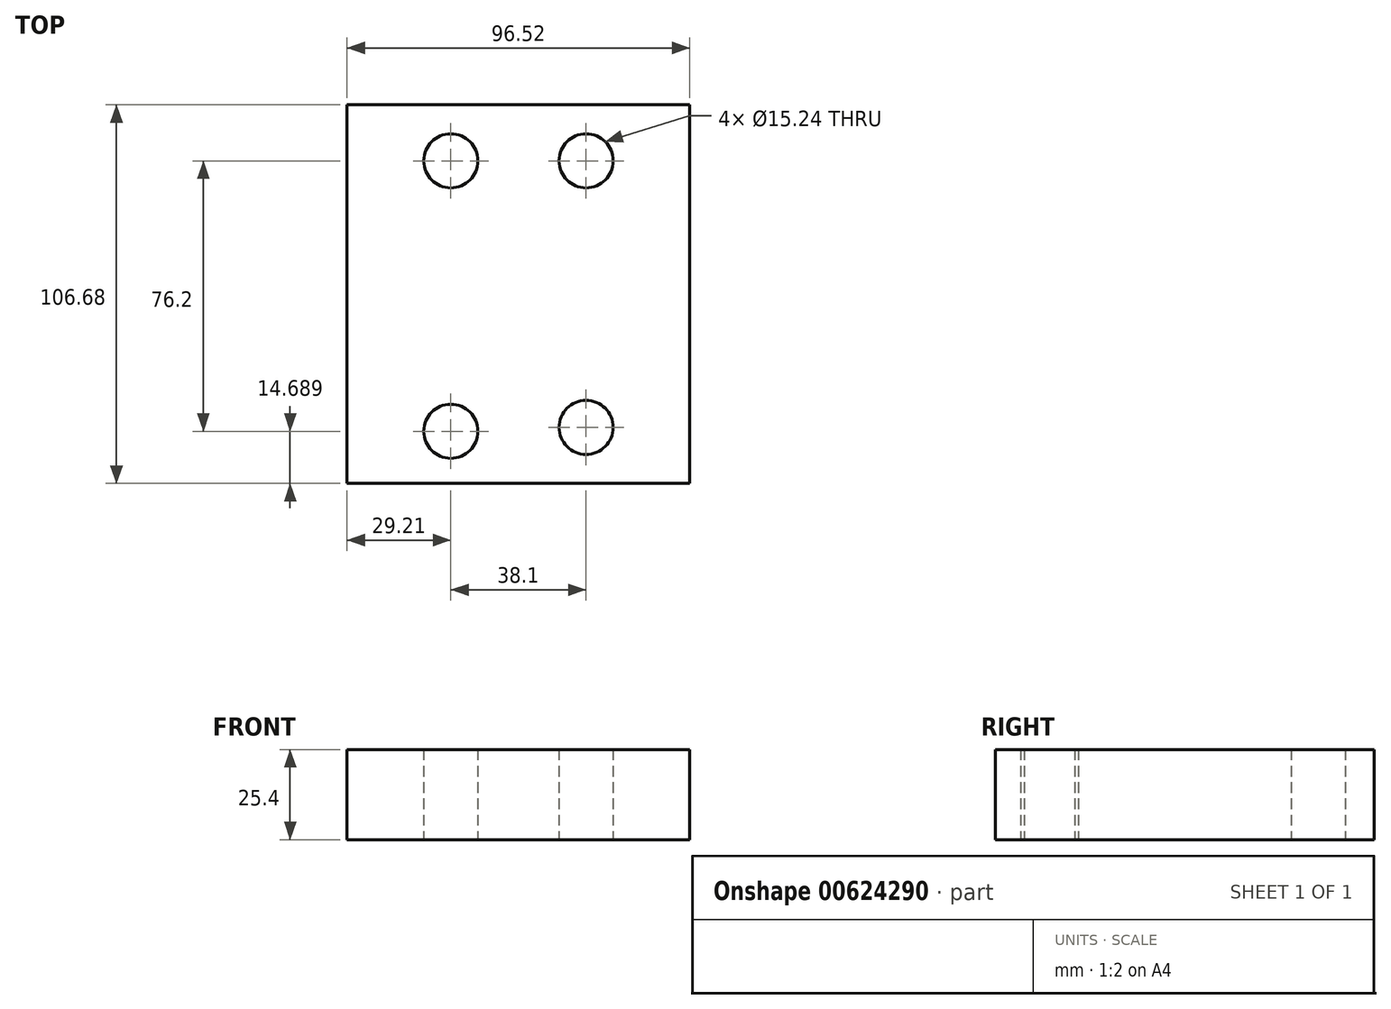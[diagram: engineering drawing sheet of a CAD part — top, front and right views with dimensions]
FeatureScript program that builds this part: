
annotation { "Feature Type Name" : "Feature", "Feature Type Description" : "" }
export const myFeature = defineFeature(function(context is Context, id is Id, definition is map)
    precondition{}
    {
        {
            var Q0;
            Q0=qCreatedBy(makeId("Top.planeOp"),FACE);
            var sketch = newSketch(context, id + "F0", { "sketchPlane" : qUnion([Q0])});
            skLineSegment(sketch, "E0.bottom", {"start": v(-48.26, 53.34) * mm, "end": v(48.26, 53.34) * mm});
            skLineSegment(sketch, "E0.top", {"start": v(-48.26, -53.34) * mm, "end": v(48.26, -53.34) * mm});
            skLineSegment(sketch, "E0.left", {"start": v(-48.26, 53.34) * mm, "end": v(-48.26, -53.34) * mm});
            skLineSegment(sketch, "E0.right", {"start": v(48.26, 53.34) * mm, "end": v(48.26, -53.34) * mm});
            skCircle(sketch, "E1", {"center": v(-19.05, 37.55) * mm, "radius": 7.62 * mm});
            skCircle(sketch, "E2", {"center": v(19.05, 37.55) * mm, "radius": 7.62 * mm});
            skCircle(sketch, "E3", {"center": v(19.05, -37.55) * mm, "radius": 7.62 * mm});
            skCircle(sketch, "E4", {"center": v(-19.05, -38.65) * mm, "radius": 7.62 * mm});
            skSolve(sketch);
        }
        {
            var Q0;
            Q0=makeQuery(id+"F0.imprint","IMPRINT",FACE,{"disambiguationData":[TD([[makeQuery(id+"F0.imprint","IMPRINT",EDGE,{"derivedFrom":sQuery(id+"F0.wireOp",EDGE,"E0.bottom")}),-1.0]])]});
            extrude(context, id + "F1", {"entities" : qUnion([Q0]), "depth" : 25.4 * mm, "offsetDistance" : 25.4 * mm});
        }
    });
